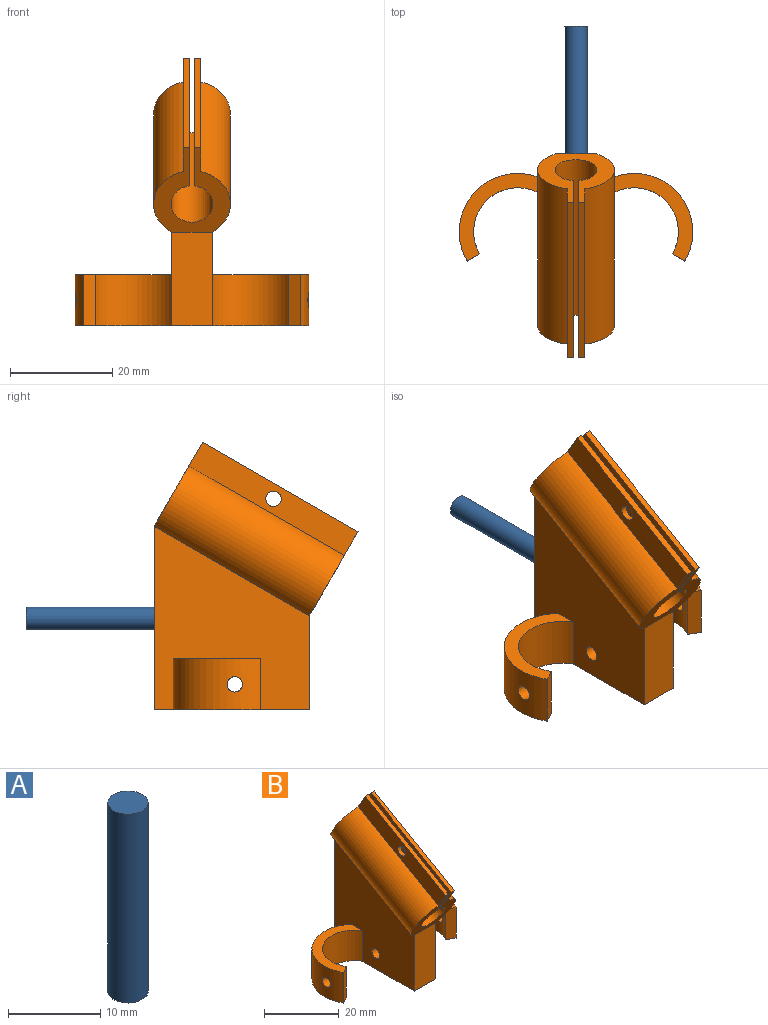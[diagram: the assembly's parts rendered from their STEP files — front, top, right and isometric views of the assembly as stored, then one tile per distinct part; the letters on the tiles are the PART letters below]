
ASSEMBLY  parts=2 mates=1
PART A: 3 faces, bbox 4.4x4.4x25 mm
  f0: cylinder r=2.18mm len=25mm, axis (0,0,-1), area 342.3mm2, adj f1,f2
  f1: plane 4.36x4.36mm, normal (0,0,1), area 14.9mm2, adj f0
  f2: plane 4.36x4.36mm, normal (0,0,-1), area 14.9mm2, adj f0
PART B: 29 faces, bbox 45.6x39.8x52.3 mm
  f0: cylinder r=11.4mm len=18.8mm, axis (0,0,-1), area 312.2mm2, adj f4,f18,f22,f23,f27
  f1: cylinder r=8.6mm len=16mm, axis (0,0,-1), area 262.1mm2, adj f4,f18,f22,f23,f27
  f2: cylinder r=11.4mm len=18.8mm, axis (0,0,-1), area 312.2mm2, adj f18,f19,f24,f25,f26
  f3: cylinder r=8.6mm len=16mm, axis (0,0,-1), area 262.1mm2, adj f18,f19,f24,f25,f26
  f4: plane 35.82x30.31mm, normal (-1,0,0), area 770.6mm2, adj f0,f1,f7,f18,f20,f21,f23,f28
  f5: plane 16.49x15mm, normal (0,0.87,0.5), area 126.9mm2, adj f7,f8,f9,f10,f11,f12,f13,f14
  f6: plane 16.49x15mm, normal (0,-0.87,-0.5), area 126.9mm2, adj f7,f8,f9,f10,f11,f12,f13,f14
  f7: cylinder r=7.5mm len=37.14mm, axis (0,-0.87,-0.5), area 617mm2, adj f4,f5,f6,f13
  f8: cylinder r=4.1mm len=34.4mm, axis (0,-0.87,-0.5), area 866.5mm2, adj f5,f6,f9,f15
  f9: plane 34.63x24.97mm, normal (-1,0,0), area 295mm2, adj f5,f6,f8,f10,f17
  f10: plane 30.31x17.5mm, normal (0,-0.5,0.87), area 42mm2, adj f5,f6,f9,f11
  f11: plane 33.01x22.17mm, normal (1,0,0), area 181.8mm2, adj f5,f6,f10,f12,f17
  f12: cylinder r=7.5mm len=37.14mm, axis (0,-0.87,-0.5), area 617mm2, adj f5,f6,f11,f19
  f13: plane 33.01x22.17mm, normal (-1,0,0), area 181.8mm2, adj f5,f6,f7,f14,f16
  f14: plane 30.31x17.5mm, normal (0,-0.5,0.87), area 42mm2, adj f5,f6,f13,f15
  f15: plane 34.63x24.97mm, normal (1,0,0), area 295mm2, adj f5,f6,f8,f14,f16
  f16: cylinder r=1.5mm len=3mm, axis (-1,0,0), area 11.3mm2, adj f13,f15
  f17: cylinder r=1.5mm len=3mm, axis (-1,0,0), area 11.3mm2, adj f9,f11
  f18: plane 45.6x30.31mm, normal (0,0,-1), area 406.7mm2, adj f0,f1,f2,f3,f4,f19,f20,f21
  f19: plane 35.82x30.31mm, normal (1,0,0), area 770.6mm2, adj f2,f3,f12,f18,f20,f21,f25,f28
  f20: plane 18.32x8mm, normal (0,-1,0), area 146.6mm2, adj f4,f6,f18,f19
  f21: plane 35.82x8mm, normal (0,1,0), area 286.6mm2, adj f4,f5,f18,f19
  f22: plane 10x2.43mm, normal (0.5,-0.87,0), area 28mm2, adj f0,f1,f18,f23
  f23: plane 18.8x17.1mm, normal (0,0,1), area 82.1mm2, adj f0,f1,f4,f22
  f24: plane 10x2.43mm, normal (-0.5,-0.87,0), area 28mm2, adj f2,f3,f18,f25
  f25: plane 18.8x17.1mm, normal (0,0,1), area 82.1mm2, adj f2,f3,f19,f24
  f26: cylinder r=1.5mm len=3.07mm, axis (1,0,0), area 26.6mm2, adj f2,f3
  f27: cylinder r=1.5mm len=3.07mm, axis (1,0,0), area 26.6mm2, adj f0,f1
  f28: cylinder r=1.5mm len=8mm, axis (1,0,0), area 75.4mm2, adj f4,f19
PLACE A rot(axis=(-1,0,0),90deg) t=(-32.21,53.82,106.81)mm
PLACE B t=(-32.21,26.8,53.9)mm
MATE ball A.f0 <-> B.f21  axis (0,-1,0) through (-32.21,53.82,106.81)mm
